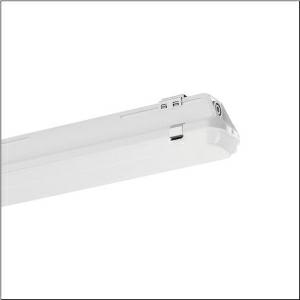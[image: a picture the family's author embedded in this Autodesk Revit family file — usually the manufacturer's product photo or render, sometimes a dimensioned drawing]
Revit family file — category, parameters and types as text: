
# Revit family: monsun_r__21_51fb10mp680b_ab58
name_source: partatom
category: Lighting Fixtures
units: mm (PartAtom-declared; Revit-internal decimal feet)

## family parameters
Cut with Voids When Loaded = No
Host = Face
Light Source = No
Part Type = Normal
Room Calculation Point = No
Round Connector Dimension = Use Diameter
Shared = No

## types (1)
- --- (1 x LED, 8190 lm, 53.6 W, 6500K)
    Apparent Load = 54 VA
    CIE Flux Codes = 47 77 93 94 100
    Color Rendering = 80
    Color Temperature = 6500K
    Default Elevation = 1800 mm
    Description = Monsun® 21, damp-proof luminaire, chain hanger, primary optical cover: enclosure, of PMMA, light emission: direct distribution, primary light characteristic: symmetric, installation type: suspended mounting, surface-mounted, horizontal mounting, vertical mounting, LED, rated luminous flux: 8.190lm, luminous efficacy: 153lm/W, light colour: 865, colour temperature: 6500K, control gear: ECG, with terminal, 3-pole, max. 2.5mm², mains connection: 220..240V, AC, 50/60Hz, rated input power: 54W, housing, of glass-fibre reinforced polyester, uncoated, bright grey, length: 1.590mm, width: 90mm, height: 88mm, clip for enclosure, of stainless steel (V2A), ceiling mounting element, of stainless steel (V2A), chain hanger, of stainless steel (V2A), protection rating (complete): IP66, insulation class (complete): insulation class I (protective earthing), certification: CE, ENEC, VDE, UKCA, protection symbol: D, impact resistance: IK04, permissible operating ambient temperature: -25..+35°C, standard: EN 50419, EN 60598-2-1, corresponds to IFS (International Featured Standards) requirements for safety and quality in the food industry, for indoor or canopied outdoor use, no direct snow, no direct sun, no direct rain, packaging unit: 1 piece
    Height = 89 mm
    Lamp = 1 x LED
    Lamp Light Flux = 8190 lm
    Lamp Power = 53.6 W
    Lamp count = 1
    Length = 1590 mm
    Luminous efficacy = 153 lm/W
    Manufacturer = Siteco
    ModVariant = No
    Model = 51FB10MP680B
    Mounting Place = Ceiling
    Mounting Type = Pendant
    Number of Poles = 1
    OnlyDefault = Yes
    Power Factor = 1
    Product Name = Monsun® 21
    Product group = damp-proof luminaire | ceiling pendant
    ProductGroupID = 908
    Protection Class = Protection class I
    Protection Degree = IP 66
    RLX_Detail_Level = 1
    RlxData = <blob elided: 89313 chars, md5=1a69372d>
    Socket = socket
    Standby Power = 0 W
    System Light Flux = 8190 lm
    System Power = 54 W
    Type Comments = factory setting: luminous flux: 100 % | (A | C | E) | 121 mA
    Type Image = l_1006717.jpg
    URL = http://relux.com
    VarID = @adj_056899
    Voltage = 0 V
    Weight = 0.00 kg
    Width = 90 mm

## geometry (parser evidence)
native form markers: Blend x4, Sweep x11
no freeform markers — native parametric forms only
